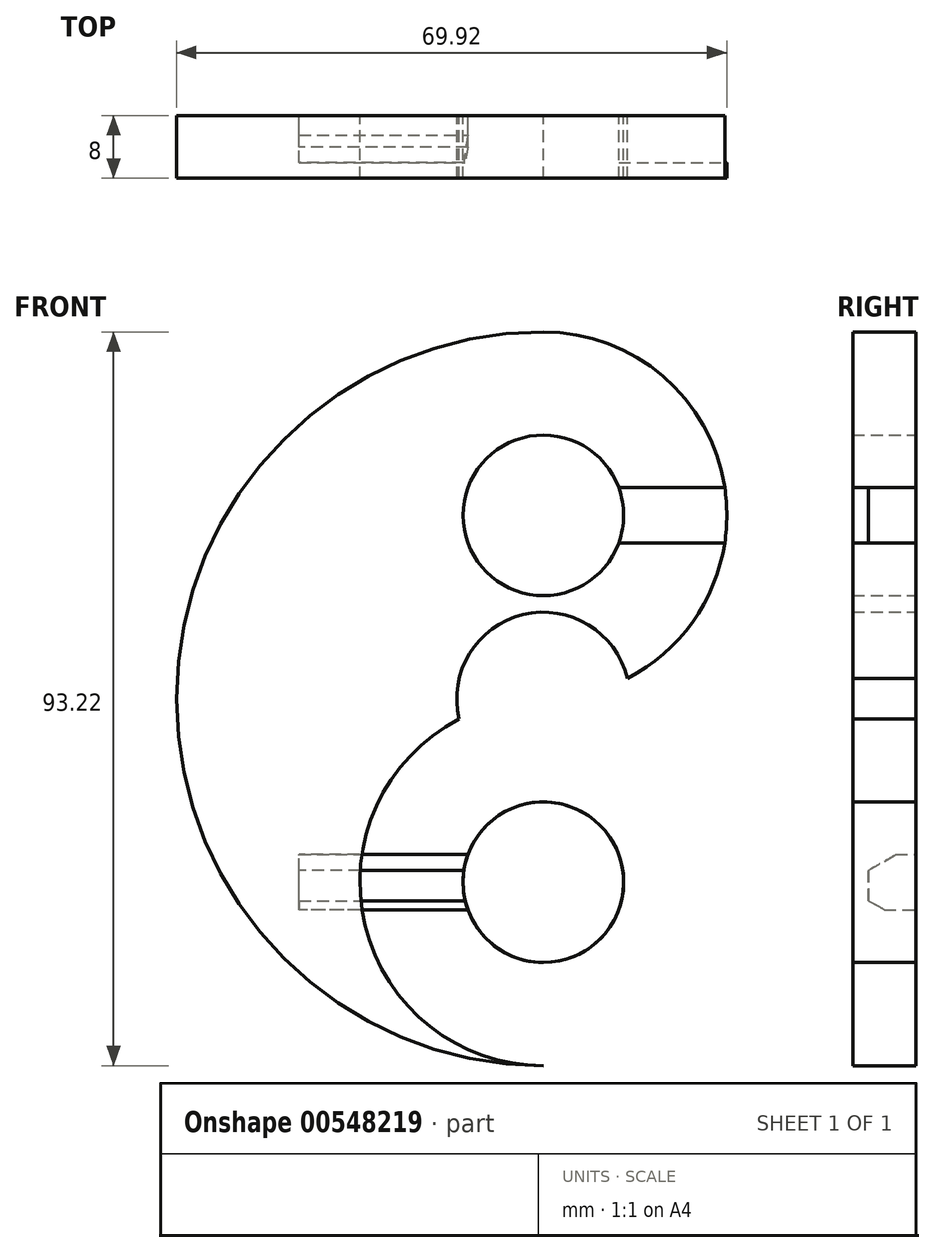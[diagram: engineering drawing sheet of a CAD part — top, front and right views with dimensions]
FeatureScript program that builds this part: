
annotation { "Feature Type Name" : "Feature", "Feature Type Description" : "" }
export const myFeature = defineFeature(function(context is Context, id is Id, definition is map)
    precondition{}
    {
        {
            var Q0;
            Q0=qCreatedBy(makeId("Front.planeOp"),FACE);
            var sketch = newSketch(context, id + "F0", { "sketchPlane" : qUnion([Q0])});
            skArc(sketch, "E0", {"start": v(0, 0) * mm, "mid": v(23.3, 23.3) * mm, "end": v(0, 46.61) * mm});
            skArc(sketch, "E1", {"start": v(0, 0) * mm, "mid": v(-23.3, -23.3) * mm, "end": v(0, -46.61) * mm});
            skCircle(sketch, "E2", {"center": v(0, 23.3) * mm, "radius": 10.2 * mm});
            skArc(sketch, "E3", {"start": v(0, 46.61) * mm, "mid": v(-46.61, 0) * mm, "end": v(0, -46.61) * mm});
            skCircle(sketch, "E4", {"center": v(0, -23.3) * mm, "radius": 10.2 * mm});
            skLineSegment(sketch, "E5", {"start": v(0, -23.3) * mm, "end": v(-31.02, -23.3) * mm});
            skPoint(sketch, "E6.middle", {"position": v(-15.5, -23.3) * mm});
            skCircle(sketch, "E7", {"center": v(0, 0) * mm, "radius": 11 * mm});
            skPoint(sketch, "E8", {"position": v(10.69, 2.6) * mm});
            skPoint(sketch, "E9", {"position": v(-10.69, -2.6) * mm});
            skLineSegment(sketch, "E10", {"start": v(0, 23.3) * mm, "end": v(31.02, 23.3) * mm});
            skPoint(sketch, "E11", {"position": v(15.5, 23.3) * mm});
            skLineSegment(sketch, "E12.bottom", {"start": v(0, 26.8) * mm, "end": v(31.02, 26.8) * mm});
            skLineSegment(sketch, "E12.top", {"start": v(0, 19.8) * mm, "end": v(31.02, 19.8) * mm});
            skLineSegment(sketch, "E12.left", {"start": v(0, 26.8) * mm, "end": v(0, 19.8) * mm});
            skLineSegment(sketch, "E12.right", {"start": v(31.02, 26.8) * mm, "end": v(31.02, 19.8) * mm});
            skSolve(sketch);
        }
        {
            var Q0;
            Q0=qCreatedBy(makeId("Front.planeOp"),FACE);
            var sketch = newSketch(context, id + "F1", { "sketchPlane" : qUnion([Q0])});
            skLineSegment(sketch, "E13.bottom", {"start": v(0, -26.8) * mm, "end": v(-31.02, -26.8) * mm});
            skLineSegment(sketch, "E13.top", {"start": v(0, -19.8) * mm, "end": v(-31.02, -19.8) * mm});
            skLineSegment(sketch, "E13.left", {"start": v(0, -26.8) * mm, "end": v(0, -19.8) * mm});
            skLineSegment(sketch, "E13.right", {"start": v(-31.02, -26.8) * mm, "end": v(-31.02, -19.8) * mm});
            skPoint(sketch, "E13.middle", {"position": v(-15.5, -23.3) * mm});
            skSolve(sketch);
        }
        {
            var Q0;
            Q0=makeQuery(id+"F1.imprint","IMPRINT",FACE,{"disambiguationData":[TD([[makeQuery(id+"F1.imprint","IMPRINT",EDGE,{"derivedFrom":sQuery(id+"F1.wireOp",EDGE,"E13.bottom")}),-1.0]])]});
            extrude(context, id + "F2", {"entities" : qUnion([Q0]), "depth" : 6 * mm, "offsetDistance" : 25.4 * mm});
        }
        {
            var Q0;
            Q0=makeQuery(id+"F0.imprint","IMPRINT",FACE,{"disambiguationData":[TD([[makeQuery(id+"F0.imprint","IMPRINT",EDGE,{"derivedFrom":sQuery(id+"F0.wireOp",EDGE,"E2")}),-1.0]])]});
            var Q1;
            Q1=makeQuery(id+"F0.imprint","IMPRINT",FACE,{"disambiguationData":[TD([[makeQuery(id+"F0.imprint","IMPRINT",EDGE,{"derivedFrom":sQuery(id+"F0.wireOp",EDGE,"E4")}),1.0]])]});
            extrude(context, id + "F3", {"entities" : qUnion([Q0, Q1]), "operationType" : NewBodyOperationType.ADD, "depth" : 8 * mm, "offsetDistance" : 25.4 * mm});
        }
        {
            var Q0;
            Q0=makeQuery(id+"F2.opExtrude","CAP_EDGE",EDGE,{"disambiguationData":[OSD([sQuery(id+"F1.wireOp",EDGE,"E13.top")])],"isStart":false});
            chamfer(context, id + "F4", {"entities" : qUnion([Q0]), "chamferType" : ChamferType.OFFSET_ANGLE, "width" : 2 * mm, "oppositeDirection" : false, "angle" : 60 * degree, "tangentPropagation" : true});
        }
        {
            var Q0;
            Q0=makeQuery(id+"F2.opExtrude","CAP_EDGE",EDGE,{"disambiguationData":[OSD([sQuery(id+"F1.wireOp",EDGE,"E13.bottom")])],"isStart":false});
            chamfer(context, id + "F5", {"entities" : qUnion([Q0]), "chamferType" : ChamferType.OFFSET_ANGLE, "width" : 2 * mm, "oppositeDirection" : false, "angle" : 30 * degree, "tangentPropagation" : true});
        }
        {
            var Q0;
            {var subQ0=sQuery(id+"F0.wireOp",EDGE,"E12.bottom");var subQ1=sQuery(id+"F0.wireOp",EDGE,"E0");var subQ2=makeQuery(id+"F0.imprint","INTERSECT",VERTEX,{"derivedFrom":[subQ1,subQ0]});Q0=makeQuery(id+"F0.imprint","IMPRINT",FACE,{"disambiguationData":[TD([[makeQuery(id+"F0.imprint","IMPRINT",EDGE,{"disambiguationData":[TD([[subQ2,1.0]])],"derivedFrom":subQ1}),-1.0]])]});}
            var Q1;
            {var subQ0=sQuery(id+"F0.wireOp",EDGE,"E12.top");var subQ1=sQuery(id+"F0.wireOp",EDGE,"E0");var subQ2=makeQuery(id+"F0.imprint","INTERSECT",VERTEX,{"derivedFrom":[subQ1,subQ0]});Q1=makeQuery(id+"F0.imprint","IMPRINT",FACE,{"disambiguationData":[TD([[makeQuery(id+"F0.imprint","IMPRINT",EDGE,{"disambiguationData":[TD([[subQ2,-1.0]])],"derivedFrom":subQ1}),-1.0]])]});}
            var Q2;
            {var subQ0=sQuery(id+"F0.wireOp",EDGE,"E12.bottom");var subQ1=sQuery(id+"F0.wireOp",EDGE,"E0");var subQ2=makeQuery(id+"F0.imprint","INTERSECT",VERTEX,{"derivedFrom":[subQ1,subQ0]});Q2=makeQuery(id+"F0.imprint","IMPRINT",FACE,{"disambiguationData":[TD([[makeQuery(id+"F0.imprint","IMPRINT",EDGE,{"disambiguationData":[TD([[subQ2,1.0]])],"derivedFrom":subQ1}),1.0]])]});}
            var Q3;
            {var subQ0=sQuery(id+"F0.wireOp",EDGE,"E12.top");var subQ1=sQuery(id+"F0.wireOp",EDGE,"E0");var subQ2=makeQuery(id+"F0.imprint","INTERSECT",VERTEX,{"derivedFrom":[subQ1,subQ0]});Q3=makeQuery(id+"F0.imprint","IMPRINT",FACE,{"disambiguationData":[TD([[makeQuery(id+"F0.imprint","IMPRINT",EDGE,{"disambiguationData":[TD([[subQ2,-1.0]])],"derivedFrom":subQ1}),1.0]])]});}
            var Q4;
            {var subQ0=sQuery(id+"F0.wireOp",EDGE,"E10");var subQ1=sQuery(id+"F0.wireOp",EDGE,"E2");var subQ2=makeQuery(id+"F0.imprint","INTERSECT",VERTEX,{"derivedFrom":[subQ1,subQ0]});Q4=makeQuery(id+"F0.imprint","IMPRINT",FACE,{"disambiguationData":[TD([[makeQuery(id+"F0.imprint","IMPRINT",EDGE,{"disambiguationData":[TD([[subQ2,1.0]])],"derivedFrom":subQ1}),1.0]])]});}
            var Q5;
            {var subQ0=sQuery(id+"F0.wireOp",EDGE,"E12.bottom");var subQ1=sQuery(id+"F0.wireOp",EDGE,"E2");var subQ2=makeQuery(id+"F0.imprint","INTERSECT",VERTEX,{"derivedFrom":[subQ1,subQ0]});Q5=makeQuery(id+"F0.imprint","IMPRINT",FACE,{"disambiguationData":[TD([[makeQuery(id+"F0.imprint","IMPRINT",EDGE,{"disambiguationData":[TD([[subQ2,1.0]])],"derivedFrom":subQ1}),1.0]])]});}
            extrude(context, id + "F6", {"entities" : qUnion([Q0, Q1, Q2, Q3, Q4, Q5]), "operationType" : NewBodyOperationType.REMOVE, "depth" : 6 * mm, "offsetDistance" : 25.4 * mm});
        }
        {
            var Q0;
            {var subQ0=sQuery(id+"F0.wireOp",EDGE,"E3");Q0=makeQuery(id+"F0.imprint","IMPRINT",FACE,{"disambiguationData":[TD([[makeQuery(id+"F0.imprint","IMPRINT",EDGE,{"derivedFrom":subQ0}),1.0]])]});}
            var Q1;
            Q1=makeQuery(id+"F0.imprint","IMPRINT",FACE,{"disambiguationData":[TD([[makeQuery(id+"F0.imprint","IMPRINT",EDGE,{"derivedFrom":sQuery(id+"F0.wireOp",EDGE,"E4")}),1.0]])]});
            extrude(context, id + "F7", {"entities" : qUnion([Q0, Q1]), "depth" : 8 * mm, "offsetDistance" : 25.4 * mm});
        }
    });
